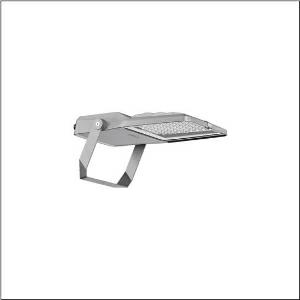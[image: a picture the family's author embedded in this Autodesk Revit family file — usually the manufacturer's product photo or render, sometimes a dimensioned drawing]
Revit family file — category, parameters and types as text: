
# Revit family: floodlight_fl_21_mini___pl52_5xa7775b2d1a_29c3
name_source: partatom
category: Lighting Fixtures
units: mm (PartAtom-declared; Revit-internal decimal feet)

## family parameters
Cut with Voids When Loaded = No
Host = Face
Light Source = No
Part Type = Normal
Room Calculation Point = No
Round Connector Dimension = Use Diameter
Shared = No

## types (1)
- --- (1 x LED, 6230 lm, 45.7 W, 3000K)
    Apparent Load = 46 VA
    CIE Flux Codes = 26 60 98 100 100
    Color Rendering = 70
    Color Temperature = 3000K
    Default Elevation = 1800 mm
    Description = Floodlight FL 21 mini, floodlight, primary light control with lens, of PMMA, primary optical cover: protective disc, of toughened safety glass, transparent, light distribution: PL52, light emission: direct distribution, installation type: surface-mounted, LED, High Power LED, rated luminous flux: 6.230lm, luminous efficacy: 136lm/W, light colour: 730, colour temperature: 3000K, control gear: Smart Interface (Zhaga), control: flexible luminous flux parameterisation, time-dependent luminous flux control, constant luminous flux control, overheat protection, pre-setting: logarithmic dimming characteristic, with terminal, 6-pole, mains connection: 220..240V, AC, 50/60Hz, start of lifetime: 46W, end of service life: 48W, reduction: 22W, luminaire housing, of diecast aluminium, powder-coated, SITECO metallic grey (DB 702S), corrosivity category C5 mid according to DIN EN ISO 12944, suitable for swimming pools, chlorine-resistant, sealing non-destructively replaceable, mounting bracket, of steel, galvanised, powder-coated, SITECO metallic grey (DB 702S), Smart Interface above, protection rating (complete): IP66, insulation class (complete): insulation class II (safety insulation), certification: CE, ENEC, VDE, protection symbol: D, impact resistance: IK08, permissible operating ambient temperature: -40..+40°C, permissible operating ambient temperature for outdoor applications: -40..+50°C, standard: DIN EN 12944, LABS conformity tested according to VDMA 24364:2018-05, packaging unit: 1 piece

Light Distribution: PL52
    Height = 70 mm
    Lamp = 1 x LED
    Lamp Light Flux = 6230 lm
    Lamp Power = 45.7 W
    Lamp count = 1
    Length = 485 mm
    Luminous efficacy = 136 lm/W
    Manufacturer = Siteco
    ModVariant = No
    Model = 5XA7775B2D1A
    Number of Poles = 1
    OnlyDefault = Yes
    Power Factor = 1
    Product Name = Floodlight FL 21 mini | PL52
    Product group = floodlight | pylon annexe
    ProductGroupID = 6201
    Protection Class = Protection class II
    Protection Degree = IP 66
    RLX_Detail_Level = 1
    RLX_Emergency_Light_Flux = 0 lm
    RLX_Emergency_Type = 0
    RLX_Emergency_Type_DB = No
    RlxData = <blob elided: 96169 chars, md5=674ab69a>
    Socket = socket
    Standby Power = 0 W
    System Light Flux = 6230 lm
    System Power = 46 W
    Type Comments = factory setting: luminous flux: 100 % | dim-lin: 254 | 463 mA
    Type Image = l_1006845.jpg
    URL = http://relux.com
    VarID = @adj_162957
    Voltage = 0 V
    Weight = 0.00 kg
    Width = 337 mm

## geometry (parser evidence)
native form markers: Blend x4, Sweep x12
no freeform markers — native parametric forms only
